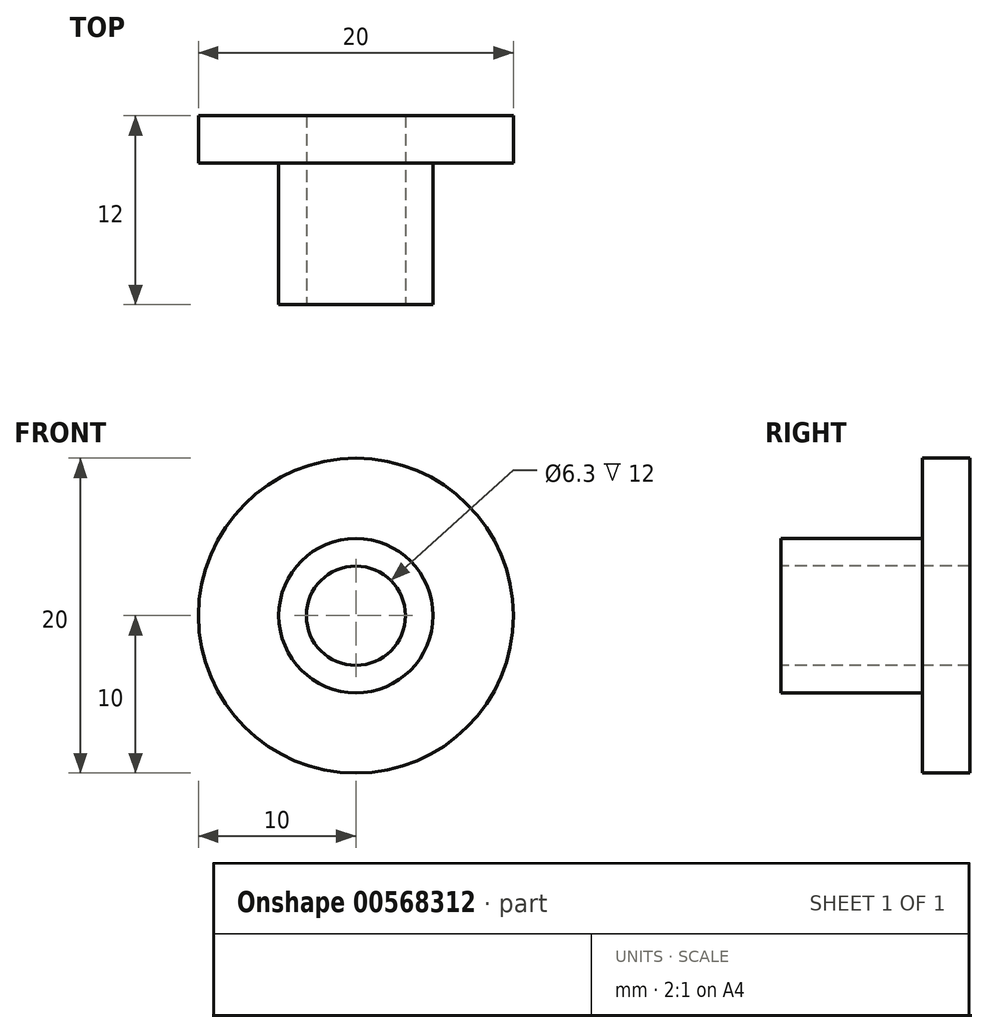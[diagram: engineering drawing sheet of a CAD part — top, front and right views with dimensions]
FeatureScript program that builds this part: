
annotation { "Feature Type Name" : "Feature", "Feature Type Description" : "" }
export const myFeature = defineFeature(function(context is Context, id is Id, definition is map)
    precondition{}
    {
        {
            var Q0;
            Q0=qCreatedBy(makeId("Front.planeOp"),FACE);
            var sketch = newSketch(context, id + "F0", { "sketchPlane" : qUnion([Q0])});
            skCircle(sketch, "E0", {"center": v(0, 0) * mm, "radius": 10 * mm});
            skCircle(sketch, "E1", {"center": v(0, 0) * mm, "radius": 3.15 * mm});
            skSolve(sketch);
        }
        {
            var Q0;
            Q0 = qSketchRegion(id + "F0", true);
            extrude(context, id + "F1", {"entities" : qUnion([Q0]), "oppositeDirection" : true, "depth" : 12 * mm, "offsetDistance" : 25 * mm});
        }
        {
            var Q0;
            Q0=makeQuery(id+"F1.opExtrude","CAP_FACE",FACE,{"disambiguationData":[OSD([sQuery(id+"F0.wireOp",EDGE,"E0"),sQuery(id+"F0.wireOp",EDGE,"E1")])],"isStart":true});
            var sketch = newSketch(context, id + "F2", { "sketchPlane" : qUnion([Q0])});
            skCircle(sketch, "E2", {"center": v(0, 0) * mm, "radius": 4.9 * mm});
            skSolve(sketch);
        }
        {
            var Q0;
            Q0=makeQuery(id+"F2.imprint","IMPRINT",FACE,{"disambiguationData":[TD([[makeQuery(id+"F2.imprint","IMPRINT",EDGE,{"derivedFrom":sQuery(id+"F2.wireOp",EDGE,"E2")}),-1.0]])]});
            extrude(context, id + "F3", {"entities" : qUnion([Q0]), "operationType" : NewBodyOperationType.REMOVE, "oppositeDirection" : true, "depth" : 9 * mm, "offsetDistance" : 25 * mm});
        }
    });
